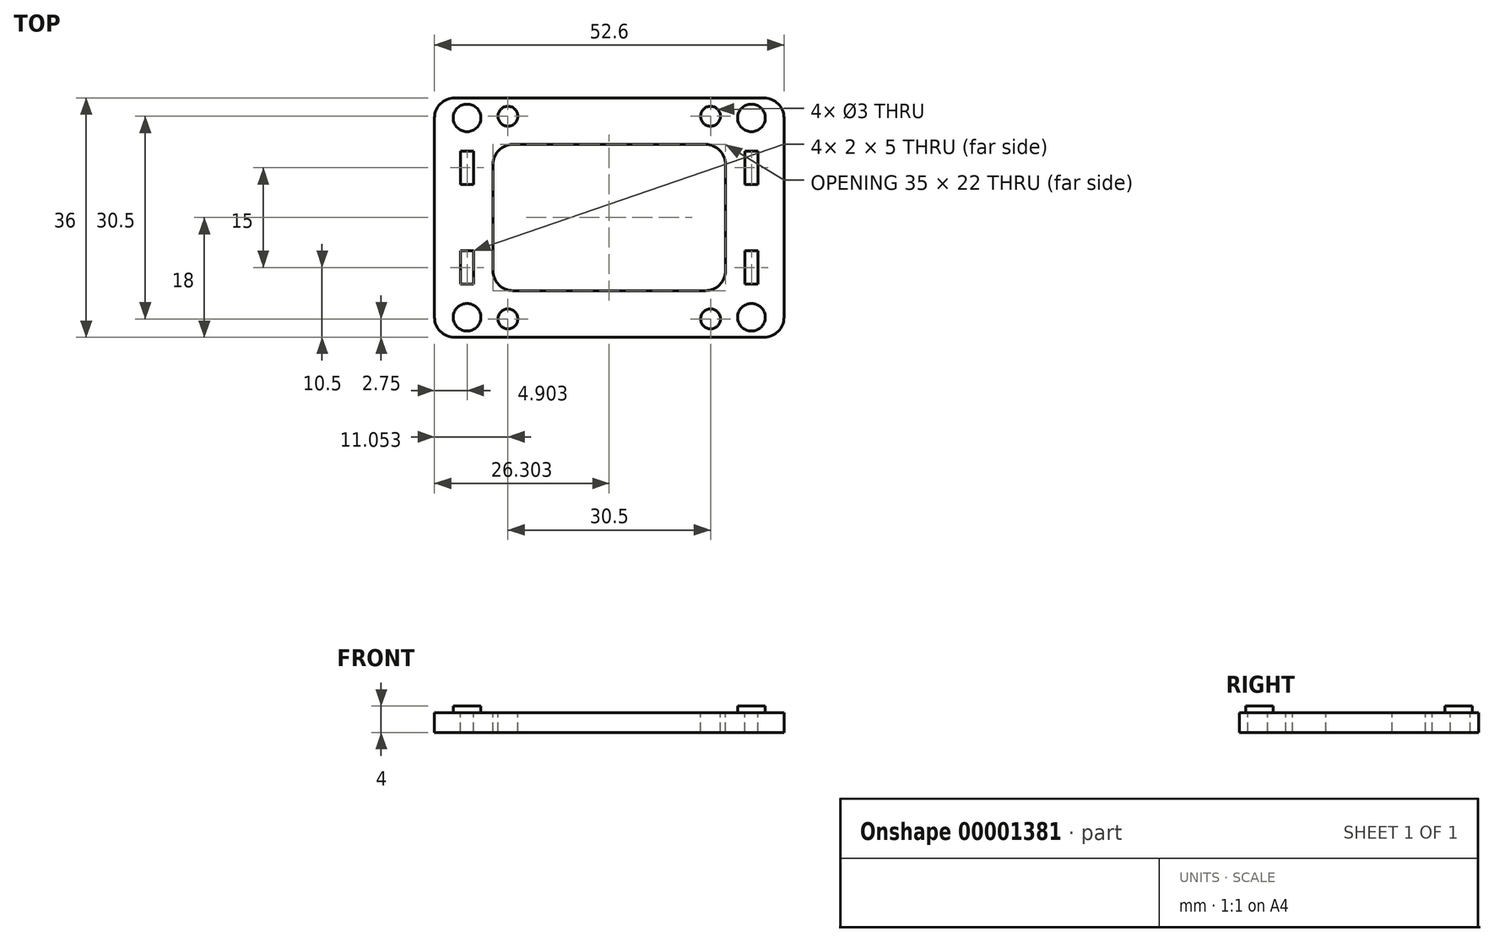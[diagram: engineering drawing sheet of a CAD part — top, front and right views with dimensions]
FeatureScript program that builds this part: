
annotation { "Feature Type Name" : "Feature", "Feature Type Description" : "" }
export const myFeature = defineFeature(function(context is Context, id is Id, definition is map)
    precondition{}
    {
        {
            var Q0;
            Q0=qCreatedBy(makeId("Top.planeOp"),FACE);
            var sketch = newSketch(context, id + "F0", { "sketchPlane" : qUnion([Q0])});
            skLineSegment(sketch, "E0.bottom", {"start": v(-30.65, 22.16) * mm, "end": v(21.95, 22.16) * mm});
            skLineSegment(sketch, "E0.top", {"start": v(-30.65, -13.84) * mm, "end": v(21.95, -13.84) * mm});
            skLineSegment(sketch, "E0.left", {"start": v(-30.65, 22.16) * mm, "end": v(-30.65, -13.84) * mm});
            skLineSegment(sketch, "E0.right", {"start": v(21.95, 22.16) * mm, "end": v(21.95, -13.84) * mm});
            skSolve(sketch);
        }
        {
            var Q0;
            Q0 = qSketchRegion(id + "F0", true);
            extrude(context, id + "F1", {"entities" : qUnion([Q0]), "depth" : 3 * mm});
        }
        {
            var Q0;
            Q0=makeQuery(id+"F1.opExtrude","CAP_FACE",FACE,{"disambiguationData":[OSD([sQuery(id+"F0.wireOp",EDGE,"E0.bottom"),sQuery(id+"F0.wireOp",EDGE,"E0.top"),sQuery(id+"F0.wireOp",EDGE,"E0.left"),sQuery(id+"F0.wireOp",EDGE,"E0.right")])],"isStart":false});
            var sketch = newSketch(context, id + "F2", { "sketchPlane" : qUnion([Q0])});
            skCircle(sketch, "E1", {"center": v(-25.75, 19.16) * mm, "radius": 2.08 * mm});
            skCircle(sketch, "E2", {"center": v(17.05, 19.16) * mm, "radius": 2.08 * mm});
            skCircle(sketch, "E3", {"center": v(17.05, -10.84) * mm, "radius": 2.08 * mm});
            skCircle(sketch, "E4", {"center": v(-25.75, -10.84) * mm, "radius": 2.08 * mm});
            skSolve(sketch);
        }
        {
            var Q0;
            Q0 = qSketchRegion(id + "F2", true);
            extrude(context, id + "F3", {"entities" : qUnion([Q0]), "operationType" : NewBodyOperationType.ADD, "depth" : 1 * mm});
        }
        {
            var Q0;
            Q0=makeQuery(id+"F1.opExtrude","CAP_FACE",FACE,{"disambiguationData":[OSD([sQuery(id+"F0.wireOp",EDGE,"E0.bottom"),sQuery(id+"F0.wireOp",EDGE,"E0.top"),sQuery(id+"F0.wireOp",EDGE,"E0.left"),sQuery(id+"F0.wireOp",EDGE,"E0.right")])],"isStart":false});
            var sketch = newSketch(context, id + "F4", { "sketchPlane" : qUnion([Q0])});
            skLineSegment(sketch, "E5", {"start": v(-25.75, 19.16) * mm, "end": v(-25.75, -10.84) * mm, "construction": true});
            skLineSegment(sketch, "E6", {"start": v(-25.75, -10.84) * mm, "end": v(17.05, -10.84) * mm, "construction": true});
            skLineSegment(sketch, "E7", {"start": v(17.05, -10.84) * mm, "end": v(17.05, 19.16) * mm, "construction": true});
            skLineSegment(sketch, "E8", {"start": v(17.05, 19.16) * mm, "end": v(-25.75, 19.16) * mm, "construction": true});
            skLineSegment(sketch, "E9.bottom", {"start": v(-26.75, 14.16) * mm, "end": v(-24.75, 14.16) * mm});
            skLineSegment(sketch, "E9.top", {"start": v(-26.75, 9.16) * mm, "end": v(-24.75, 9.16) * mm});
            skLineSegment(sketch, "E9.left", {"start": v(-26.75, 14.16) * mm, "end": v(-26.75, 9.16) * mm});
            skLineSegment(sketch, "E9.right", {"start": v(-24.75, 14.16) * mm, "end": v(-24.75, 9.16) * mm});
            skLineSegment(sketch, "E10", {"start": v(-25.75, 4.16) * mm, "end": v(17.05, 4.16) * mm, "construction": true});
            skLineSegment(sketch, "E11", {"start": v(-4.35, 19.16) * mm, "end": v(-4.35, -10.84) * mm, "construction": true});
            skLineSegment(sketch, "E12.0.MirrorCS", {"start": v(18.05, 9.16) * mm, "end": v(16.05, 9.16) * mm});
            skLineSegment(sketch, "E12.1.MirrorCS", {"start": v(18.05, 14.16) * mm, "end": v(16.05, 14.16) * mm});
            skLineSegment(sketch, "E12.2.MirrorCS", {"start": v(18.05, 14.16) * mm, "end": v(18.05, 9.16) * mm});
            skLineSegment(sketch, "E12.3.MirrorCS", {"start": v(16.05, 14.16) * mm, "end": v(16.05, 9.16) * mm});
            skLineSegment(sketch, "E13.0.MirrorCS", {"start": v(16.05, -5.84) * mm, "end": v(16.05, -0.84) * mm});
            skLineSegment(sketch, "E13.1.MirrorCS", {"start": v(18.05, -0.84) * mm, "end": v(16.05, -0.84) * mm});
            skLineSegment(sketch, "E13.2.MirrorCS", {"start": v(18.05, -5.84) * mm, "end": v(16.05, -5.84) * mm});
            skLineSegment(sketch, "E13.3.MirrorCS", {"start": v(18.05, -5.84) * mm, "end": v(18.05, -0.84) * mm});
            skLineSegment(sketch, "E13.4.MirrorCS", {"start": v(-26.75, -5.84) * mm, "end": v(-24.75, -5.84) * mm});
            skLineSegment(sketch, "E13.5.MirrorCS", {"start": v(-24.75, -5.84) * mm, "end": v(-24.75, -0.84) * mm});
            skLineSegment(sketch, "E13.6.MirrorCS", {"start": v(-26.75, -5.84) * mm, "end": v(-26.75, -0.84) * mm});
            skLineSegment(sketch, "E13.7.MirrorCS", {"start": v(-26.75, -0.84) * mm, "end": v(-24.75, -0.84) * mm});
            skSolve(sketch);
        }
        {
            var Q0;
            Q0 = qSketchRegion(id + "F4", true);
            extrude(context, id + "F5", {"entities" : qUnion([Q0]), "operationType" : NewBodyOperationType.REMOVE, "oppositeDirection" : true, "depth" : 25 * mm});
        }
        {
            var Q0;
            Q0=makeQuery(id+"F1.opExtrude","CAP_FACE",FACE,{"disambiguationData":[OSD([sQuery(id+"F0.wireOp",EDGE,"E0.bottom"),sQuery(id+"F0.wireOp",EDGE,"E0.top"),sQuery(id+"F0.wireOp",EDGE,"E0.left"),sQuery(id+"F0.wireOp",EDGE,"E0.right")])],"isStart":false});
            var sketch = newSketch(context, id + "F6", { "sketchPlane" : qUnion([Q0])});
            skCircle(sketch, "E14", {"center": v(-19.6, 19.41) * mm, "radius": 1.5 * mm});
            skCircle(sketch, "E15", {"center": v(10.9, 19.41) * mm, "radius": 1.5 * mm});
            skCircle(sketch, "E16", {"center": v(-19.6, -11.09) * mm, "radius": 1.5 * mm});
            skCircle(sketch, "E17", {"center": v(10.9, -11.09) * mm, "radius": 1.5 * mm});
            skLineSegment(sketch, "E18.bottom", {"start": v(-18.85, 15.16) * mm, "end": v(10.15, 15.16) * mm});
            skLineSegment(sketch, "E18.top", {"start": v(-18.85, -6.84) * mm, "end": v(10.15, -6.84) * mm});
            skLineSegment(sketch, "E18.left", {"start": v(-21.85, 12.16) * mm, "end": v(-21.85, -3.84) * mm});
            skLineSegment(sketch, "E18.right", {"start": v(13.15, 12.16) * mm, "end": v(13.15, -3.84) * mm});
            skPoint(sketch, "E19.visualSharp", {"position": v(-21.85, 15.16) * mm});
            skArc(sketch, "E19.filletArc", {"start": v(-18.85, 15.16) * mm, "mid": v(-20.97, 14.28) * mm, "end": v(-21.85, 12.16) * mm});
            skPoint(sketch, "E20.visualSharp", {"position": v(-21.85, -6.84) * mm});
            skArc(sketch, "E20.filletArc", {"start": v(-21.85, -3.84) * mm, "mid": v(-20.97, -5.96) * mm, "end": v(-18.85, -6.84) * mm});
            skPoint(sketch, "E21.visualSharp", {"position": v(13.15, -6.84) * mm});
            skArc(sketch, "E21.filletArc", {"start": v(10.15, -6.84) * mm, "mid": v(12.27, -5.96) * mm, "end": v(13.15, -3.84) * mm});
            skPoint(sketch, "E22.visualSharp", {"position": v(13.15, 15.16) * mm});
            skArc(sketch, "E22.filletArc", {"start": v(13.15, 12.16) * mm, "mid": v(12.27, 14.28) * mm, "end": v(10.15, 15.16) * mm});
            skSolve(sketch);
        }
        {
            var Q0;
            Q0 = qSketchRegion(id + "F6", true);
            extrude(context, id + "F7", {"entities" : qUnion([Q0]), "operationType" : NewBodyOperationType.REMOVE, "oppositeDirection" : true, "depth" : 25 * mm});
        }
        {
            var Q0;
            Q0=makeQuery(id+"F1.opExtrude","SWEPT_EDGE",EDGE,{"disambiguationData":[OSD([sQuery(id+"F0.wireOp",EDGE,"E0.top"),sQuery(id+"F0.wireOp",EDGE,"E0.left")])]});
            var Q1;
            Q1=makeQuery(id+"F1.opExtrude","SWEPT_EDGE",EDGE,{"disambiguationData":[OSD([sQuery(id+"F0.wireOp",EDGE,"E0.top"),sQuery(id+"F0.wireOp",EDGE,"E0.right")])]});
            var Q2;
            Q2=makeQuery(id+"F1.opExtrude","SWEPT_EDGE",EDGE,{"disambiguationData":[OSD([sQuery(id+"F0.wireOp",EDGE,"E0.bottom"),sQuery(id+"F0.wireOp",EDGE,"E0.right")])]});
            var Q3;
            Q3=makeQuery(id+"F1.opExtrude","SWEPT_EDGE",EDGE,{"disambiguationData":[OSD([sQuery(id+"F0.wireOp",EDGE,"E0.bottom"),sQuery(id+"F0.wireOp",EDGE,"E0.left")])]});
            fillet(context, id + "F8", {"entities" : qUnion([Q0, Q1, Q2, Q3]), "radius" : 3 * mm, "tangentPropagation" : true, "allowEdgeOverflow" : false});
        }
    });
